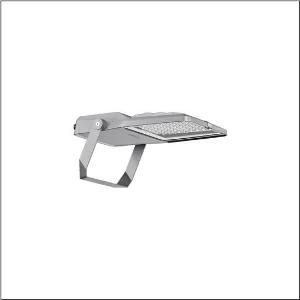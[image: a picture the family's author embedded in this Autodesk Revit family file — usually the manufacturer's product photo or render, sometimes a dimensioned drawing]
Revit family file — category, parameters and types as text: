
# Revit family: floodlight_fl_21_iq_mini___pl43_5xa7772b4a1a_cc8f
name_source: partatom
category: Lighting Fixtures
units: mm (PartAtom-declared; Revit-internal decimal feet)

## family parameters
Cut with Voids When Loaded = No
Host = Face
Light Source = No
Part Type = Normal
Room Calculation Point = No
Round Connector Dimension = Use Diameter
Shared = No

## types (1)
- --- (1 x LED, 6660 lm, 45.5 W, 4000K)
    Apparent Load = 46 VA
    CIE Flux Codes = 27 78 99 100 100
    Color Rendering = 70
    Color Temperature = 4000K
    Default Elevation = 1800 mm
    Description = Floodlight FL 21 iQ mini, floodlight, primary light control with lens, of PMMA, primary optical cover: protective disc, of toughened safety glass, transparent, light distribution: PL43, light emission: direct distribution, installation type: surface-mounted, lamps: LED, High Power LED, rated values: 6.660lm | 45,5W | 146,4lm/W (begin service life); end service life: 6.660lm | 48W; at 50% lumin. flux: 3.330lm | 21,5W | 154,9lm/W, colour temperature: 4000K, colour rendering: CRI > 70, light colour: 740, light setting 1 begin service life: 100% | 6.660lm | 45,5W | 146,4lm/W | 4.000K, light setting 1 end service life: 48W, further light settings possible, control: Street-Remote, Auto-Match, Temp-Guard, Night-Set, Smart-Wire, Desk-Remote (wireless, voltage-free reading and setting of iQ features in the workshop via application-optimized NFC function/RFID function), optimised constant luminous flux control (CLO 2.0), pre-setting: linear dimming characteristic, with terminal, 6-pole, mains connection: 220..240V, AC, 50/60Hz, luminaire housing, of diecast aluminium, powder-coated, SITECO metallic grey (DB 702S), corrosivity category C5 mid according to DIN EN ISO 12944suitable for swimming poolschlorine-resistant, sealing non-destructively replaceable, mounting bracket, of steel, galvanised, powder-coated, SITECO metallic grey (DB 702S), protection rating (complete): IP66, insulation class (complete): insulation class II (safety insulation), certification: CE, ENEC, VDE, protection symbol: D, impact resistance: IK08, permissible operating ambient temperature: -40..+40°C, permissible operating ambient temperature for outdoor applications: -40..+50°C, standard: DIN EN 12944, LABS conformity tested according to VDMA 24364:2018-05, packaging unit: 1 piece

Light Distribution: PL43
    Height = 70 mm
    Lamp = 1 x LED
    Lamp Light Flux = 6660 lm
    Lamp Power = 45.5 W
    Lamp count = 1
    Length = 485 mm
    Luminous efficacy = 146 lm/W
    Manufacturer = Siteco
    ModVariant = No
    Model = 5XA7772B4A1A
    Mounting Place = Pole
    Mounting Type = Pole annexe
    Number of Poles = 1
    OnlyDefault = Yes
    Power Factor = 1
    Product Name = Floodlight FL 21 iQ mini | PL43
    Product group = floodlight | pylon annexe
    ProductGroupID = 6201
    Protection Class = Protection class II
    Protection Degree = IP 66
    RLX_Detail_Level = 1
    RLX_Emergency_Light_Flux = 0 lm
    RLX_Emergency_Type = 0
    RLX_Emergency_Type_DB = No
    RlxData = <blob elided: 96153 chars, md5=0dbf621a>
    Socket = socket
    Standby Power = 0 W
    System Light Flux = 6660 lm
    System Power = 46 W
    Type Comments = factory setting: luminous flux: 100 % | dim-lin: 254 | 463 mA
    Type Image = l_1006845.jpg
    URL = http://relux.com
    VarID = @adj_162995
    Voltage = 0 V
    Weight = 0.00 kg
    Width = 337 mm

## geometry (parser evidence)
native form markers: Blend x4, Sweep x13
no freeform markers — native parametric forms only
